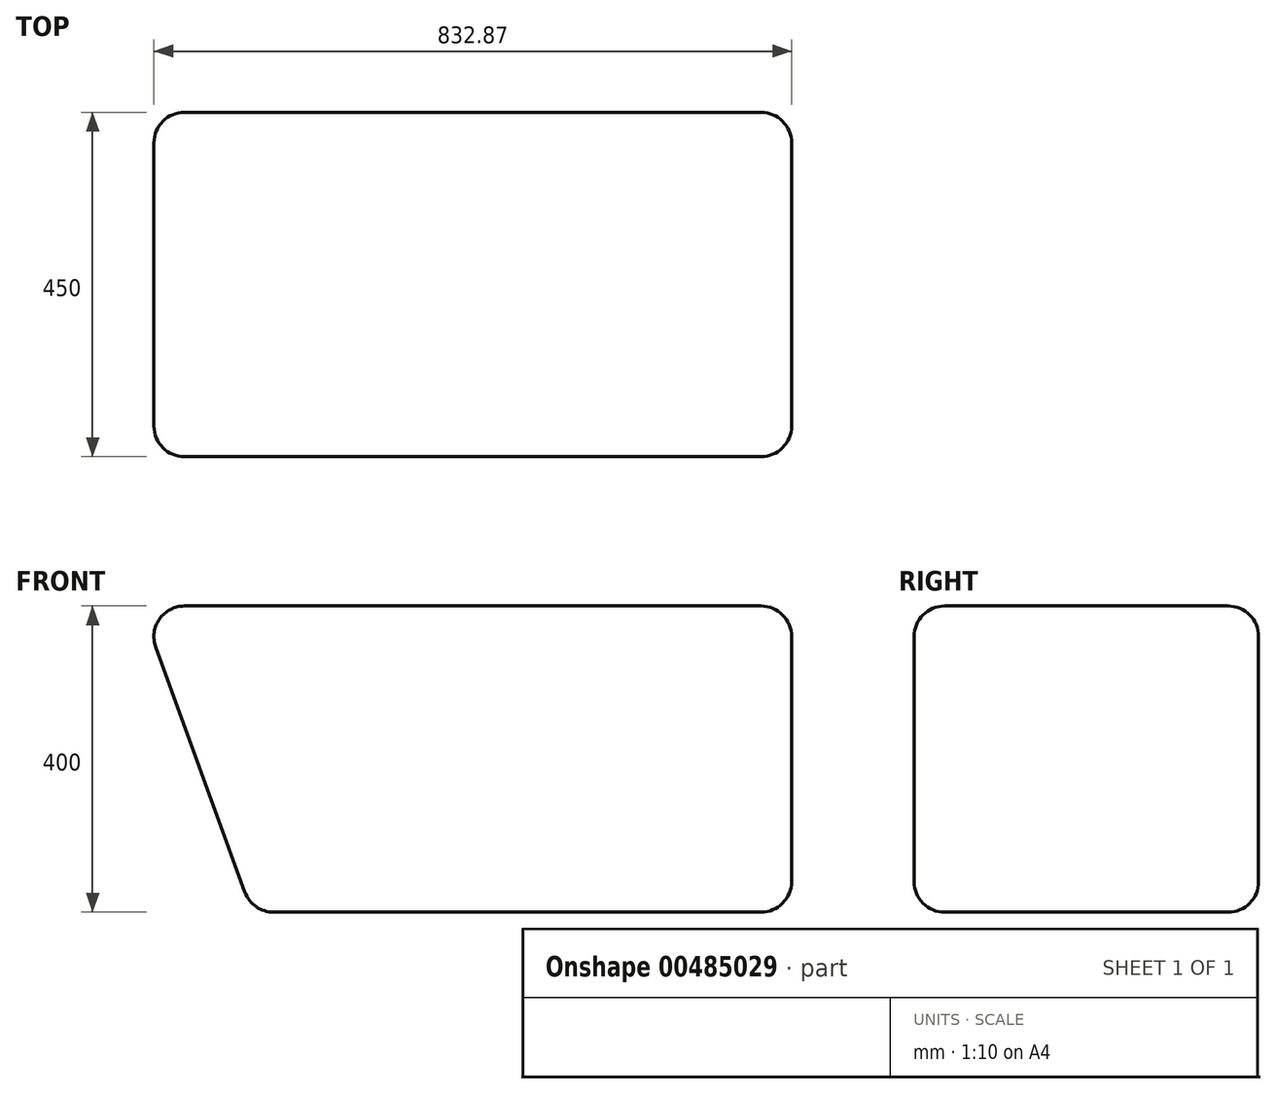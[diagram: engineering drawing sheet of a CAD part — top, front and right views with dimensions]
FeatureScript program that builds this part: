
annotation { "Feature Type Name" : "Feature", "Feature Type Description" : "" }
export const myFeature = defineFeature(function(context is Context, id is Id, definition is map)
    precondition{}
    {
        {
            var Q0;
            Q0=qCreatedBy(makeId("Front.planeOp"),FACE);
            var sketch = newSketch(context, id + "F0", { "sketchPlane" : qUnion([Q0])});
            skLineSegment(sketch, "E0", {"start": v(145.59, 0) * mm, "end": v(0, 400) * mm});
            skLineSegment(sketch, "E1", {"start": v(0, 400) * mm, "end": v(850, 400) * mm});
            skLineSegment(sketch, "E2", {"start": v(850, 400) * mm, "end": v(850, 0) * mm});
            skLineSegment(sketch, "E3", {"start": v(850, 0) * mm, "end": v(145.59, 0) * mm});
            skSolve(sketch);
        }
        {
            var Q0;
            Q0=makeQuery(id+"F0.imprint","IMPRINT",FACE,{"disambiguationData":[TD([[makeQuery(id+"F0.imprint","IMPRINT",EDGE,{"derivedFrom":sQuery(id+"F0.wireOp",EDGE,"E0")}),-1.0]])]});
            extrude(context, id + "F1", {"entities" : qUnion([Q0]), "endBound" : BoundingType.SYMMETRIC, "depth" : 450 * mm, "offsetDistance" : 25 * mm});
        }
        {
            var Q0;
            Q0=makeQuery(id+"F1.opExtrude","CAP_EDGE",EDGE,{"disambiguationData":[OSD([sQuery(id+"F0.wireOp",EDGE,"E3")])],"isStart":false});
            var Q1;
            Q1=makeQuery(id+"F1.opExtrude","SWEPT_FACE",FACE,{"disambiguationData":[OSD([sQuery(id+"F0.wireOp",EDGE,"E3")])]});
            var Q2;
            Q2=makeQuery(id+"F1.opExtrude","CAP_EDGE",EDGE,{"disambiguationData":[OSD([sQuery(id+"F0.wireOp",EDGE,"E0")])],"isStart":false});
            var Q3;
            Q3=makeQuery(id+"F1.opExtrude","SWEPT_FACE",FACE,{"disambiguationData":[OSD([sQuery(id+"F0.wireOp",EDGE,"E2")])]});
            var Q4;
            Q4=makeQuery(id+"F1.opExtrude","SWEPT_FACE",FACE,{"disambiguationData":[OSD([sQuery(id+"F0.wireOp",EDGE,"E1")])]});
            var Q5;
            Q5=makeQuery(id+"F1.opExtrude","CAP_FACE",FACE,{"disambiguationData":[OSD([sQuery(id+"F0.wireOp",EDGE,"E0"),sQuery(id+"F0.wireOp",EDGE,"E1"),sQuery(id+"F0.wireOp",EDGE,"E2"),sQuery(id+"F0.wireOp",EDGE,"E3")])],"isStart":false});
            var Q6;
            Q6=makeQuery(id+"F1.opExtrude","SWEPT_EDGE",EDGE,{"disambiguationData":[OSD([sQuery(id+"F0.wireOp",EDGE,"E1"),sQuery(id+"F0.wireOp",EDGE,"E2")])]});
            var Q7;
            Q7=makeQuery(id+"F1.opExtrude","CAP_FACE",FACE,{"disambiguationData":[OSD([sQuery(id+"F0.wireOp",EDGE,"E0"),sQuery(id+"F0.wireOp",EDGE,"E1"),sQuery(id+"F0.wireOp",EDGE,"E2"),sQuery(id+"F0.wireOp",EDGE,"E3")])],"isStart":true});
            var Q8;
            Q8=makeQuery(id+"F1.opExtrude","SWEPT_EDGE",EDGE,{"disambiguationData":[OSD([sQuery(id+"F0.wireOp",EDGE,"E0"),sQuery(id+"F0.wireOp",EDGE,"E1")])]});
            var Q9;
            Q9=makeQuery(id+"F1.opExtrude","SWEPT_FACE",FACE,{"disambiguationData":[OSD([sQuery(id+"F0.wireOp",EDGE,"E0")])]});
            var Q10;
            Q10=makeQuery(id+"F1.opExtrude","SWEPT_EDGE",EDGE,{"disambiguationData":[OSD([sQuery(id+"F0.wireOp",EDGE,"E0"),sQuery(id+"F0.wireOp",EDGE,"E3")])]});
            var Q11;
            Q11=makeQuery(id+"F1.opExtrude","CAP_EDGE",EDGE,{"disambiguationData":[OSD([sQuery(id+"F0.wireOp",EDGE,"E3")])],"isStart":true});
            var Q12;
            Q12=makeQuery(id+"F1.opExtrude","CAP_EDGE",EDGE,{"disambiguationData":[OSD([sQuery(id+"F0.wireOp",EDGE,"E2")])],"isStart":false});
            var Q13;
            Q13=makeQuery(id+"F1.opExtrude","CAP_EDGE",EDGE,{"disambiguationData":[OSD([sQuery(id+"F0.wireOp",EDGE,"E1")])],"isStart":false});
            var Q14;
            Q14=makeQuery(id+"F1.opExtrude","CAP_EDGE",EDGE,{"disambiguationData":[OSD([sQuery(id+"F0.wireOp",EDGE,"E2")])],"isStart":true});
            var Q15;
            Q15=makeQuery(id+"F1.opExtrude","CAP_EDGE",EDGE,{"disambiguationData":[OSD([sQuery(id+"F0.wireOp",EDGE,"E1")])],"isStart":true});
            var Q16;
            Q16=makeQuery(id+"F1.opExtrude","CAP_EDGE",EDGE,{"disambiguationData":[OSD([sQuery(id+"F0.wireOp",EDGE,"E0")])],"isStart":true});
            var Q17;
            Q17=makeQuery(id+"F1.opExtrude","SWEPT_EDGE",EDGE,{"disambiguationData":[OSD([sQuery(id+"F0.wireOp",EDGE,"E2"),sQuery(id+"F0.wireOp",EDGE,"E3")])]});
            fillet(context, id + "F2", {"entities" : qUnion([Q0, Q1, Q2, Q3, Q4, Q5, Q6, Q7, Q8, Q9, Q10, Q11, Q12, Q13, Q14, Q15, Q16, Q17]), "radius" : 40 * mm, "tangentPropagation" : true, "allowEdgeOverflow" : false});
        }
    });
